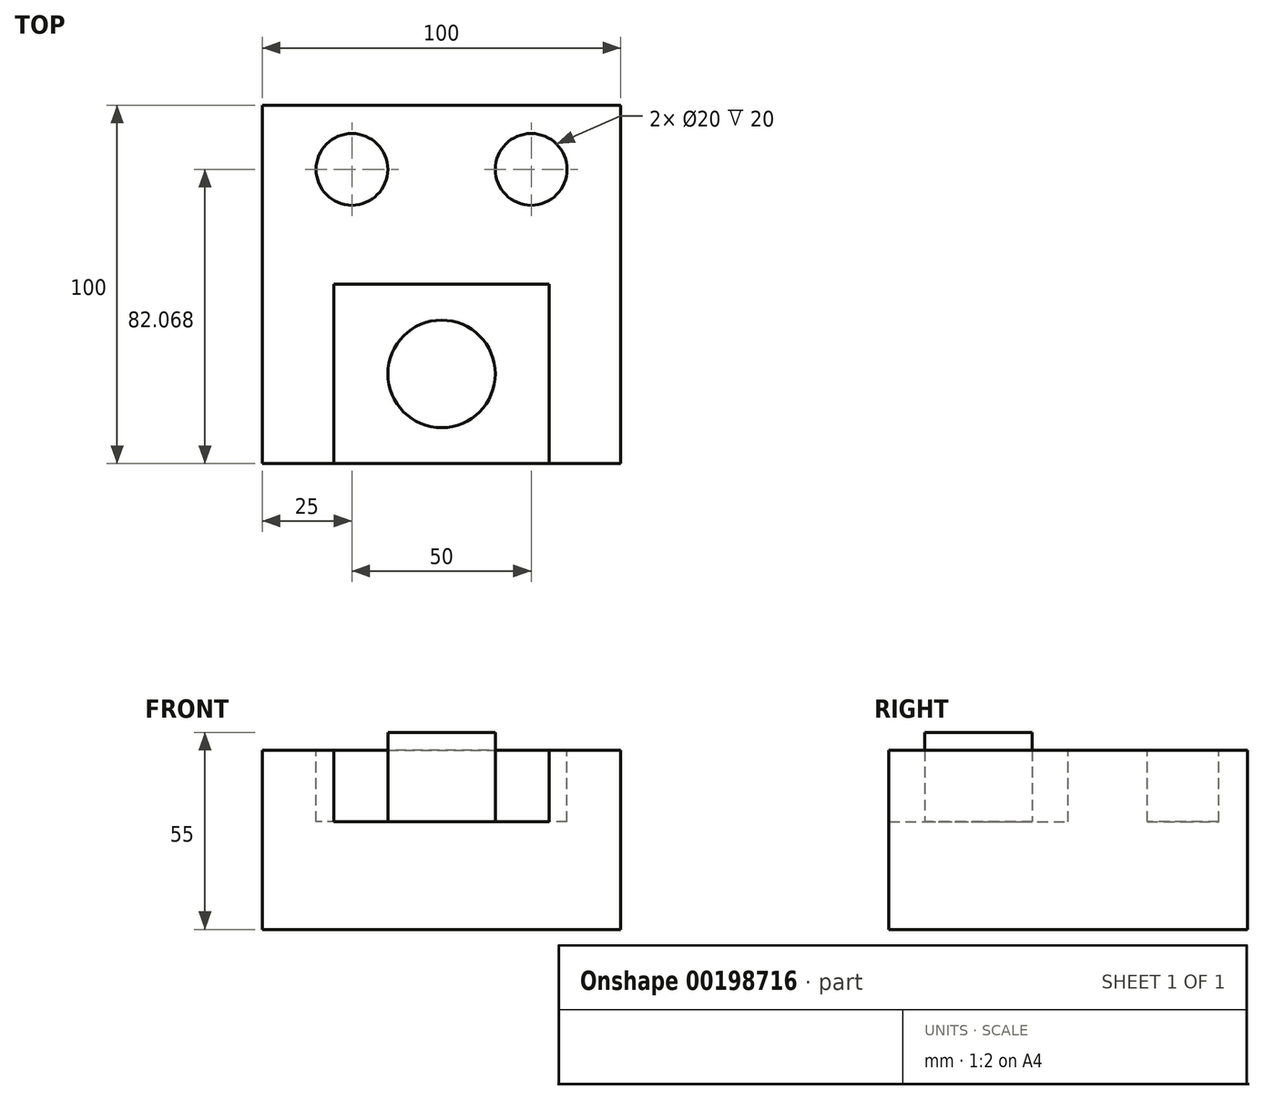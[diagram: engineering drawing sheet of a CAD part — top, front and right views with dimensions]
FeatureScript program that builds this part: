
annotation { "Feature Type Name" : "Feature", "Feature Type Description" : "" }
export const myFeature = defineFeature(function(context is Context, id is Id, definition is map)
    precondition{}
    {
        {
            var Q0;
            Q0=qCreatedBy(makeId("Top.planeOp"),FACE);
            var sketch = newSketch(context, id + "F0", { "sketchPlane" : qUnion([Q0])});
            skLineSegment(sketch, "E0.bottom", {"start": v(50, -50) * mm, "end": v(-50, -50) * mm});
            skLineSegment(sketch, "E0.top", {"start": v(50, 50) * mm, "end": v(-50, 50) * mm});
            skLineSegment(sketch, "E0.left", {"start": v(50, -50) * mm, "end": v(50, 50) * mm});
            skLineSegment(sketch, "E0.right", {"start": v(-50, -50) * mm, "end": v(-50, 50) * mm});
            skPoint(sketch, "E0.middle", {"position": v(0, 0) * mm});
            skSolve(sketch);
        }
        {
            var Q0;
            Q0=makeQuery(id+"F0.imprint","IMPRINT",FACE,{"disambiguationData":[TD([[makeQuery(id+"F0.imprint","IMPRINT",EDGE,{"derivedFrom":sQuery(id+"F0.wireOp",EDGE,"E0.bottom")}),-1.0]])]});
            extrude(context, id + "F1", {"entities" : qUnion([Q0]), "depth" : 50 * mm});
        }
        {
            var Q0;
            Q0=makeQuery(id+"F1.opExtrude","CAP_FACE",FACE,{"disambiguationData":[OSD([sQuery(id+"F0.wireOp",EDGE,"E0.bottom"),sQuery(id+"F0.wireOp",EDGE,"E0.top"),sQuery(id+"F0.wireOp",EDGE,"E0.left"),sQuery(id+"F0.wireOp",EDGE,"E0.right")])],"isStart":false});
            var sketch = newSketch(context, id + "F2", { "sketchPlane" : qUnion([Q0])});
            skLineSegment(sketch, "E1.bottom", {"start": v(-30, -50) * mm, "end": v(30, -50) * mm});
            skLineSegment(sketch, "E1.top", {"start": v(-30, 0) * mm, "end": v(30, 0) * mm});
            skLineSegment(sketch, "E1.left", {"start": v(-30, -50) * mm, "end": v(-30, 0) * mm});
            skLineSegment(sketch, "E1.right", {"start": v(30, -50) * mm, "end": v(30, 0) * mm});
            skCircle(sketch, "E2", {"center": v(-25, 32.07) * mm, "radius": 10 * mm});
            skCircle(sketch, "E3.MirrorC", {"center": v(25, 32.07) * mm, "radius": 10 * mm});
            skSolve(sketch);
        }
        {
            var Q0;
            Q0 = qSketchRegion(id + "F2", true);
            extrude(context, id + "F3", {"entities" : qUnion([Q0]), "operationType" : NewBodyOperationType.REMOVE, "oppositeDirection" : true, "depth" : 20 * mm});
        }
        {
            var Q0;
            Q0=makeQuery(id+"F3.boolean.opBoolean","COPY",FACE,{"derivedFrom":makeQuery(id+"F3.opExtrude","CAP_FACE",FACE,{"disambiguationData":[OSD([sQuery(id+"F2.wireOp",EDGE,"E1.bottom"),sQuery(id+"F2.wireOp",EDGE,"E1.top"),sQuery(id+"F2.wireOp",EDGE,"E1.left"),sQuery(id+"F2.wireOp",EDGE,"E1.right")])],"isStart":false})});
            var sketch = newSketch(context, id + "F4", { "sketchPlane" : qUnion([Q0])});
            skCircle(sketch, "E4", {"center": v(0, -25) * mm, "radius": 15 * mm});
            skPoint(sketch, "E4.centerSnap0", {"position": v(-30, -25) * mm});
            skSolve(sketch);
        }
        {
            var Q0;
            Q0=makeQuery(id+"F4.imprint","IMPRINT",FACE,{"disambiguationData":[TD([[makeQuery(id+"F4.imprint","IMPRINT",EDGE,{"derivedFrom":sQuery(id+"F4.wireOp",EDGE,"E4")}),1.0]])]});
            extrude(context, id + "F5", {"entities" : qUnion([Q0]), "operationType" : NewBodyOperationType.ADD, "depth" : 25 * mm});
        }
    });
